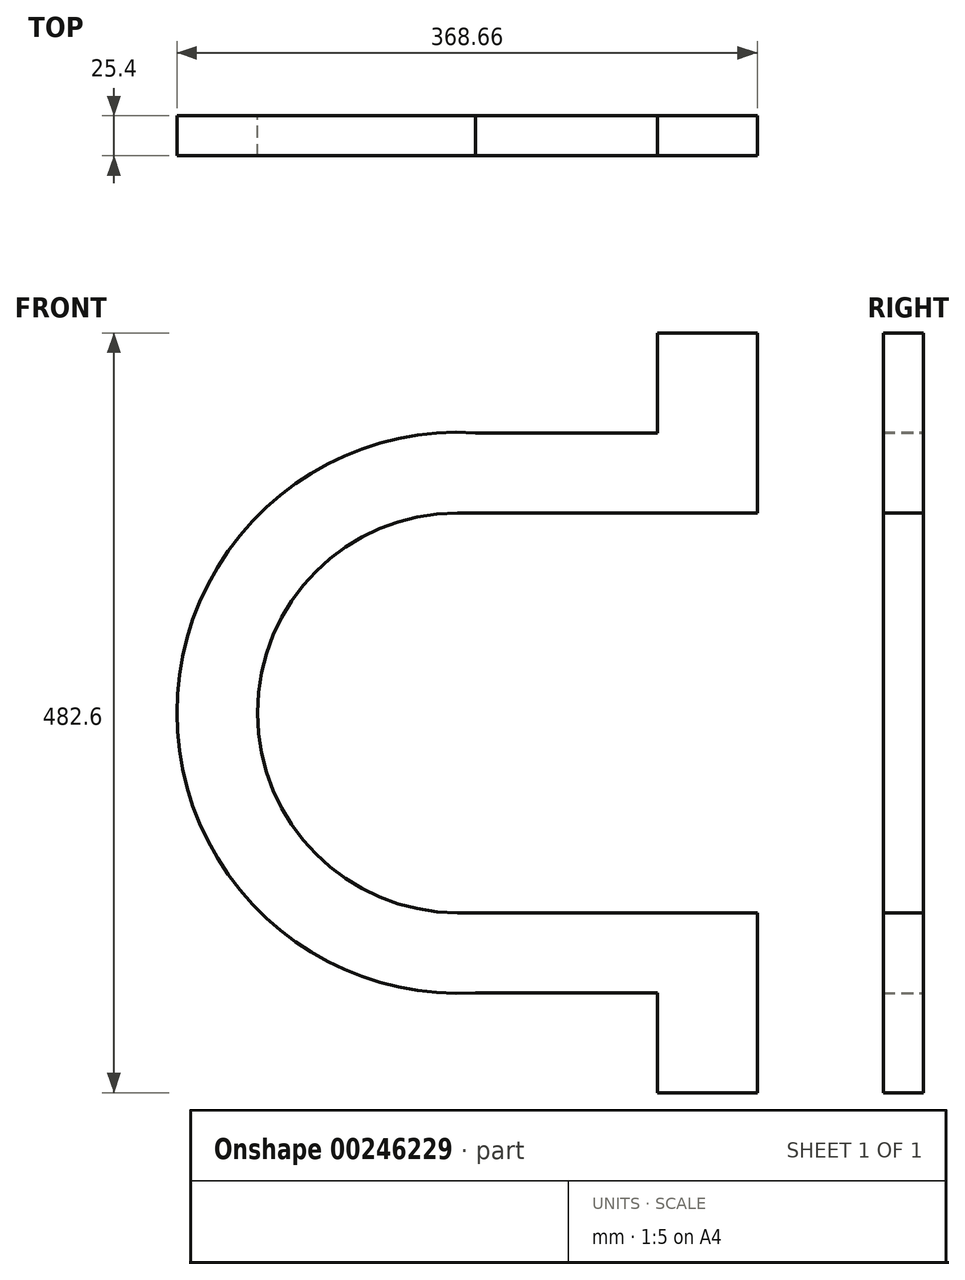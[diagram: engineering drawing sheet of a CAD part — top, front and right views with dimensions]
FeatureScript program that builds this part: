
annotation { "Feature Type Name" : "Feature", "Feature Type Description" : "" }
export const myFeature = defineFeature(function(context is Context, id is Id, definition is map)
    precondition{}
    {
        {
            var Q0;
            Q0=qCreatedBy(makeId("Front.planeOp"),FACE);
            var sketch = newSketch(context, id + "F0", { "sketchPlane" : qUnion([Q0])});
            skLineSegment(sketch, "E0.bottom", {"start": v(127, 177.8) * mm, "end": v(-11.39, 177.8) * mm});
            skLineSegment(sketch, "E0.top", {"start": v(127, -177.8) * mm, "end": v(-11.39, -177.8) * mm});
            skLineSegment(sketch, "E0.left", {"start": v(190.5, 177.8) * mm, "end": v(190.5, 127) * mm});
            skPoint(sketch, "E0.middle", {"position": v(0, 0) * mm});
            skArc(sketch, "E1", {"start": v(0, 127) * mm, "mid": v(-127, 0) * mm, "end": v(0, -127) * mm});
            skLineSegment(sketch, "E2", {"start": v(0, -127) * mm, "end": v(190.5, -127) * mm});
            skLineSegment(sketch, "E3", {"start": v(0, 127) * mm, "end": v(190.5, 127) * mm});
            skLineSegment(sketch, "E4.bottom", {"start": v(127, -127) * mm, "end": v(190.5, -127) * mm});
            skLineSegment(sketch, "E4.right", {"start": v(190.5, -127) * mm, "end": v(190.5, -177.8) * mm});
            skLineSegment(sketch, "E5.top", {"start": v(127, 127) * mm, "end": v(190.5, 127) * mm});
            skLineSegment(sketch, "E6.top", {"start": v(127, -241.3) * mm, "end": v(190.5, -241.3) * mm});
            skLineSegment(sketch, "E6.left", {"start": v(127, -177.8) * mm, "end": v(127, -241.3) * mm});
            skLineSegment(sketch, "E6.right", {"start": v(190.5, -177.8) * mm, "end": v(190.5, -241.3) * mm});
            skLineSegment(sketch, "E7.top", {"start": v(127, 241.3) * mm, "end": v(190.5, 241.3) * mm});
            skLineSegment(sketch, "E7.left", {"start": v(127, 177.8) * mm, "end": v(127, 241.3) * mm});
            skLineSegment(sketch, "E7.right", {"start": v(190.5, 177.8) * mm, "end": v(190.5, 241.3) * mm});
            skArc(sketch, "E8", {"start": v(11.39, 177.8) * mm, "mid": v(-178.16, 0) * mm, "end": v(11.39, -177.8) * mm});
            skPoint(sketch, "E9.orphan", {"position": v(-190.5, -177.8) * mm});
            skPoint(sketch, "E10.orphan", {"position": v(-190.5, 177.8) * mm});
            skSolve(sketch);
        }
        {
            var Q0;
            {var subQ0=sQuery(id+"F0.wireOp",EDGE,"E8");var subQ1=sQuery(id+"F0.wireOp",EDGE,"E0.bottom");var subQ2=makeQuery(id+"F0.imprint","INTERSECT",VERTEX,{"disambiguationData":[OD(0.0)],"derivedFrom":[subQ1,subQ0]});Q0=makeQuery(id+"F0.imprint","IMPRINT",FACE,{"disambiguationData":[TD([[makeQuery(id+"F0.imprint","IMPRINT",EDGE,{"disambiguationData":[TD([[subQ2,1.0]])],"derivedFrom":subQ1}),-1.0]])]});}
            var Q1;
            {var subQ0=sQuery(id+"F0.wireOp",EDGE,"E8");var subQ1=sQuery(id+"F0.wireOp",EDGE,"E0.top");var subQ2=makeQuery(id+"F0.imprint","INTERSECT",VERTEX,{"disambiguationData":[OD(0.0)],"derivedFrom":[subQ1,subQ0]});Q1=makeQuery(id+"F0.imprint","IMPRINT",FACE,{"disambiguationData":[TD([[makeQuery(id+"F0.imprint","IMPRINT",EDGE,{"disambiguationData":[TD([[subQ2,1.0]])],"derivedFrom":subQ1}),1.0]])]});}
            var Q2;
            Q2=makeQuery(id+"F0.imprint","IMPRINT",FACE,{"disambiguationData":[TD([[makeQuery(id+"F0.imprint","IMPRINT",EDGE,{"derivedFrom":sQuery(id+"F0.wireOp",EDGE,"E1")}),-1.0]])]});
            extrude(context, id + "F1", {"entities" : qUnion([Q0, Q1, Q2]), "depth" : 25.4 * mm});
        }
    });
